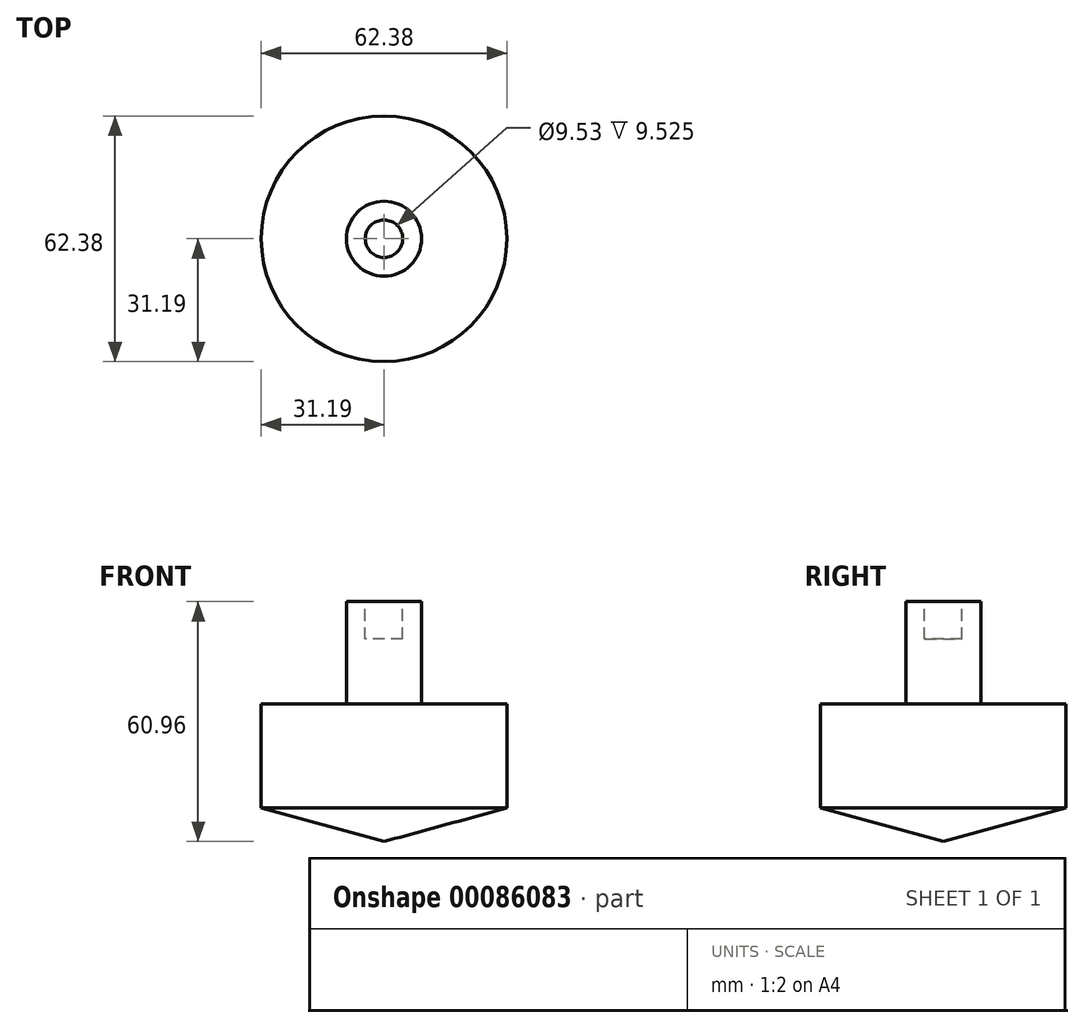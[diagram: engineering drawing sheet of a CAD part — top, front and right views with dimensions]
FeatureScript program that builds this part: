
annotation { "Feature Type Name" : "Feature", "Feature Type Description" : "" }
export const myFeature = defineFeature(function(context is Context, id is Id, definition is map)
    precondition{}
    {
        {
            var Q0;
            Q0=qCreatedBy(makeId("Front.planeOp"),FACE);
            var sketch = newSketch(context, id + "F0", { "sketchPlane" : qUnion([Q0])});
            skLineSegment(sketch, "E0", {"start": v(0, -20.8) * mm, "end": v(31.19, -12.29) * mm});
            skLineSegment(sketch, "E1", {"start": v(31.19, -12.29) * mm, "end": v(31.19, 14.18) * mm});
            skLineSegment(sketch, "E2", {"start": v(31.19, 14.18) * mm, "end": v(9.53, 14.18) * mm});
            skLineSegment(sketch, "E3", {"start": v(9.53, 14.18) * mm, "end": v(9.53, 40.17) * mm});
            skLineSegment(sketch, "E4", {"start": v(9.53, 40.17) * mm, "end": v(0, 40.17) * mm});
            skLineSegment(sketch, "E5", {"start": v(0, 40.17) * mm, "end": v(0, -20.8) * mm});
            skPoint(sketch, "E6.start.orphan", {"position": v(4.76, 40.17) * mm});
            skPoint(sketch, "E7.end.orphan", {"position": v(0, 27.7) * mm});
            skLineSegment(sketch, "E8", {"start": v(4.76, 40.17) * mm, "end": v(4.76, 30.64) * mm});
            skLineSegment(sketch, "E9", {"start": v(4.76, 30.64) * mm, "end": v(0, 30.64) * mm});
            skLineSegment(sketch, "E10", {"start": v(4.76, 40.17) * mm, "end": v(0, 40.17) * mm});
            skLineSegment(sketch, "E11", {"start": v(0, 40.17) * mm, "end": v(0, 30.64) * mm});
            skSolve(sketch);
        }
        {
            var Q0;
            Q0=makeQuery(id+"F0.imprint","IMPRINT",FACE,{"disambiguationData":[TD([[makeQuery(id+"F0.imprint","IMPRINT",EDGE,{"derivedFrom":sQuery(id+"F0.wireOp",EDGE,"E0")}),1.0]])]});
            var Q1;
            Q1=sQuery(id+"F0.wireOp",EDGE,"E5");
            revolve(context, id + "F1", {"entities" : qUnion([Q0]), "axis" : qUnion([Q1]), "revolveType" : RevolveType.FULL});
        }
    });
